# Revit family: Domotics-DomesticRanges-GEWISS-CHORUS_COMMAND-ONE-WAY_SWITCH_2M
name_source: partatom
category: Apparecchi elettrici
revit_build: Autodesk Revit 2016 (Build: 20161004_0715(x64)
units: mm (PartAtom-declared; Revit-internal decimal feet)

## family parameters
Condiviso = Sì
Host = Superficie
Mantenere orientamento annotazione = Sì
Numero OmniClass = 23.80.50.11.14
Punto di calcolo locali = Sì
Quota connettore circolare = Usa diametro
Taglio con vuoti quando caricato = Sì
Tipo di parte = Normale
Titolo OmniClass = Switches

## types (15) — shared parameters
Bidimensionale = bidimensionale interruttori 2m : GW12035
Breaking capacity: = 1.25 In (200 position changes)
Carico apparente = 0 VA
Catalogue = DOMOTICS
Catalogue Range = CHORUS - DOMESTIC RANGE
Category = One-way switch
Electrocod = 0130
Glow Wire Test = 850°C
IDF = 81fc90f9-000c-488b-bfd7-08112991af80
IDT = a07dac46-1c16-4ad8-a26d-07f4b42bbba3
Immagine tipo = GW14035.jpg
Insulation resistance = > 5 MOhm
Larghezza pulsante = 46 mm  [stored 0.150919 ft]
N. poli = 1
No. Chorus modules = 2
Produttore = GEWISS S.p.A.
Prolonged operation (no.of position changes) = 40.000 at In 250 V ac cosÃ˜=0,6
Prospetto di default = 1200 mm
Resistance at test voltage = 2000 V at 50 Hz for 1 minute
SEO = 1 way switch
Simbolo_ = SIMBOLO INTERRUTTORI : INT2PLUM
Standard; = EN 60669-1
Technical sheet = https://www.gewiss.com
Terminal grip on cable traction = > 50 N
Terminal tightening capacity flexible cables (mm2) = min. 0,75 - max. 2x4
Terminal tightening capacity rigid cables (mm2) = min. 0,5 - max. 2x2,5
Thermo-pressure with ball = 125
Tipo_ = CHORUS INTERRUTTORI 2M_BASE : GW14035 - Titanio - Illuminabile segnalazione
URL = https://www.gewiss.com
Version file RFA = 19.0
Volt = 230 V
Voltage = 250 V ac
Voltage: = 250 V ac
Wiring terminals = With screw
pulsante = GEWISS ACCIAIO BIANCO
pulsante nero = GEWISS ACCIAIO NERO

## per-type parameters (varying)
| type | Button key | Colour | Description: | Descrizione | EAN code | Modello | Number of poles | Type |
| GW14034 - 2P - Titanium | Neutral | Titanium | 2P - 16 AX | 1-WAY SWITCH, 2M 2P 16AX TITANIUM | 8011564265462 | GW14034 | 2P | General |
| GW14033 - 1P - Titanium - Illuminable | With replaceable neutral lens | Titanium | 1P - 16AX illuminable | 1-WAY SWITCH 2M 1P 16AX ILL SIG TITANIUM | 8011564265448 | GW14033 | 1P | Indicator |
| GW12035 - 2P - Black - Illuminable | With replaceable neutral lens | Black | 2P - 16AX illuminable | 1-WAY SWITCH, 2M 2P 16AX ILL SIG BLACK | 8011564266162 | GW12035 | 2P | Indicator |
| GW14035 - 2P - Titanium - Illuminable | With replaceable neutral lens | Titanium | 2P - 16AX illuminable | 1-WAY SWITCH 2M 2P 16AX ILL SIG TITANIUM | 8011564265486 | GW14035 | 2P | Indicator |
| GW10034 - 2P - White | Neutral | White | 2P - 16 AX | 1-WAY SWITCH, 2M 2P 16AX WHITE | 8011564258785 | GW10034 | 2P | General |
| GW10035 - 2P - White - Illuminable | With replaceable neutral lens | White | 2P - 16AX illuminable | 1-WAY SWITCH, 2M 2P 16AX ILL SIG WHITE | 8011564258808 | GW10035 | 2P | Indicator |
| GW10031 - 1P - White | Neutral | White | 1P - 16AX | 1-WAY SWITCH, 2M 1P 16AX WHITE | 8011564258723 | GW10031 | 1P | General |
| GW10033 - 1P - White - Illuminable | With replaceable neutral lens | White | 1P - 16AX illuminable | 1-WAY SWITCH, 2M 1P 16AX ILL SIG WHITE | 8011564258761 | GW10033 | 1P | Indicator |
| GW12031 - 1P - Black | Neutral | Black | 1P - 16AX | 1-WAY SWITCH, 2M 1P 16AX BLACK | 8011564266124 | GW12031 | 1P | General |
| GW12032 - 1P - Black - Illuminable | With diffuser | Black | 1P - 16AX illuminable | 1-WAY SWITCH, 2M 1P 16AX ILL LOC BLACK | 8011564266131 | GW12032 | 1P | Backlit |
| GW10032 - 1P - White - Illuminable | With diffuser | White | 1P - 16AX illuminable | 1-WAY SWITCH, 2M 1P 16AX ILL LOC WHITE | 8011564258747 | GW10032 | 1P | Backlit |
| GW14032 - 1P - Titanium - Illuminable | With diffuser | Titanium | 1P - 16AX illuminable | 1-WAY SWITCH 2M 1P 16AX ILL LOC TITANIUM | 8011564265424 | GW14032 | 1P | Backlit |
| GW12034 - 2P - Black | Neutral | Black | 2P - 16 AX | 1-WAY SWITCH, 2M 2P 16AX BLACK | 8011564266155 | GW12034 | 2P | General |
| GW14031 - 1P - Titanium | Neutral | Titanium | 1P - 16AX | 1-WAY SWITCH, 2M 1P 16AX TITANIUM | 8011564265400 | GW14031 | 1P | General |
| GW12033 - 1P - Black - Illuminable | With replaceable neutral lens | Black | 1P - 16AX illuminable | 1-WAY SWITCH, 2M 1P 16AX ILL SIG BLACK | 8011564266148 | GW12033 | 1P | Indicator |

note: source unit labels omitted for Thermo-pressure with ball — the stored unit's dimension contradicts the parameter name (converter mislabeling)

note: [stored X ft] marks values corroborated as IEEE doubles in the binary element streams (Revit-internal decimal feet)

## geometry (parser evidence)
native form markers: Sweep x2
no freeform markers — native parametric forms only
